# Revit family: Data_Device-Network-Leviton-Patch_Panel-Flat-110_Style
name_source: partatom
category: Data Devices
revit_build: Autodesk Revit 2018 (Build: 20170223_1515(x64)
units: mm (PartAtom-declared; Revit-internal decimal feet)

## family parameters
Cut with Voids When Loaded = No
Host = Face
Maintain Annotation Orientation = Yes
OmniClass Number = 23.85.50.17
OmniClass Title = Communication and Data Processing Equipment
Part Type = Normal
Room Calculation Point = No
Round Connector Dimension = Use Diameter
Shared = Yes

## types (1)
- Data_Device-Network-Leviton-Patch_Panel-Flat-110_Style
    Annotation Symbol is Visible = Yes
    Assembly Code = D5030600
    Date Last Modified = September 27, 2023
    Default Elevation = 24 "
    Description = Cat 6 UTP 110-Style Patch Panel, 96-Port, 4RU, black
    Die Cast = No
    Equipment Abbreviation = 110PP
    Family Version = 1.0.4
    Has ID Windows = Yes
    Manufacturer = Leviton
    Model Disclaimer = http://www.leviton.com
    Part Description = Cat 6 UTP 110-Style Patch Panel, 96-Port, 4RU, black
    Product Documentation Link = https://www.leviton.com
    Rack Spaces RU = 4
    URL = http://www.leviton.com
    Z Lateral Support = No
    z 1 Y Offset 1 = 0.16 "
    z 1 Y Offset 2 = 1.5 "
    z 12 Port Numbers = No
    z Connector Type = Data_Device-Network-Leviton-Connector-Copper-110_Style : CAT 6
    z Depth = 0.075 "
    z Has 12 Ports = Yes
    z Has 24 Ports = Yes
    z Has 48 Ports = Yes
    z Has 96 Ports = Yes
    z Has ID Windows 12 Ports = Yes
    z Has ID Windows 24 Ports = Yes
    z Has ID Windows 48 Ports = Yes
    z Has Magnifying Label 24 Ports = No
    z Has Magnifying Label 48 Ports = No
    z Height = 6.975 "
    z Length = 0.25 "
    z Leviton Type = 244
    z Mangment Bar Height = 4.25 "
    z Offset 1 = 0.075 "
    z Offset 2 = 0.425 "
    z Offset 3 = 0.5 "
    z Offset 4 = 0 "

## geometry (parser evidence)
native form markers: Blend x52, Sweep x12
no freeform markers — native parametric forms only
